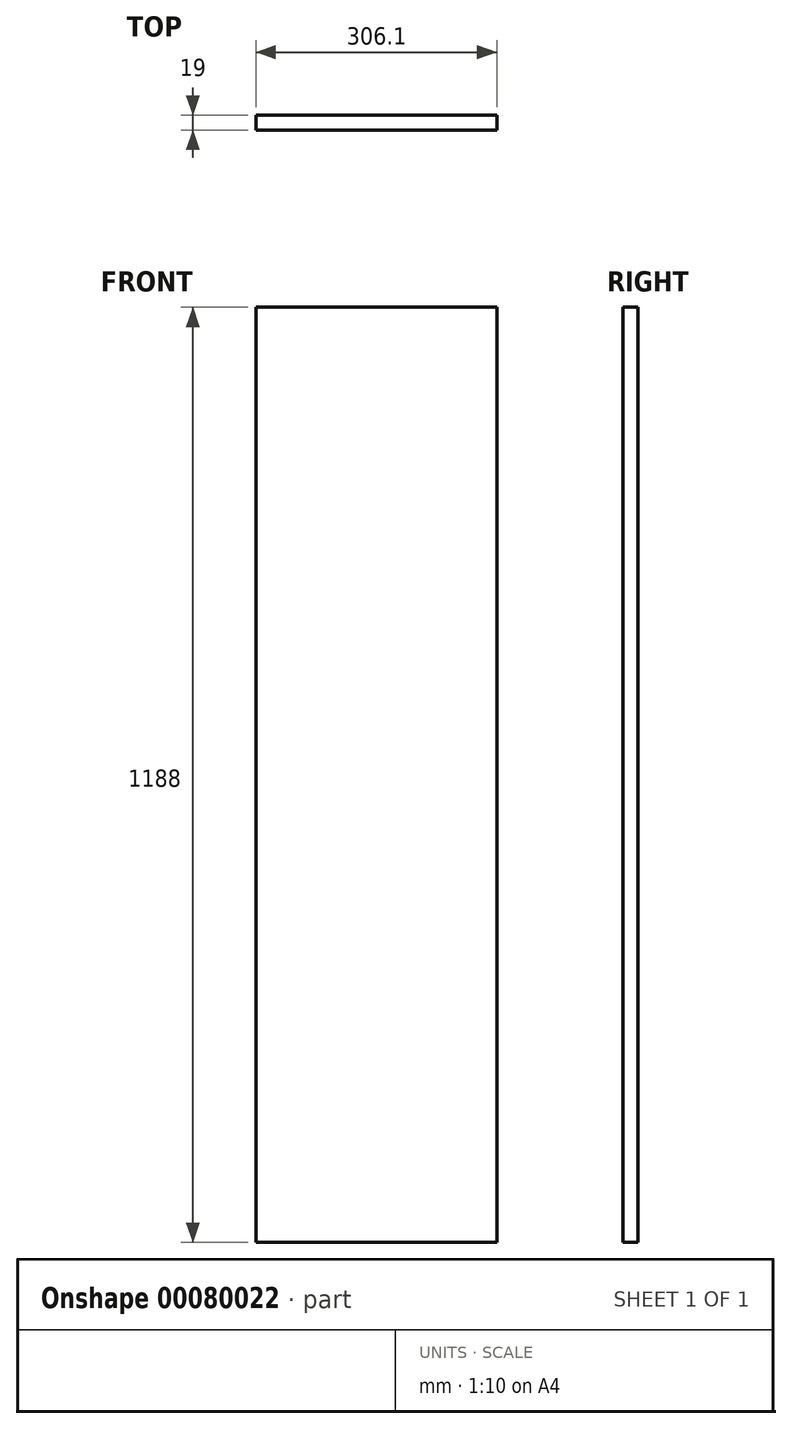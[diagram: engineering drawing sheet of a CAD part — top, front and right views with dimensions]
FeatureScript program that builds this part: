
annotation { "Feature Type Name" : "Feature", "Feature Type Description" : "" }
export const myFeature = defineFeature(function(context is Context, id is Id, definition is map)
    precondition{}
    {
        {
            var Q0;
            Q0=qCreatedBy(makeId("Front.planeOp"),FACE);
            var sketch = newSketch(context, id + "F0", { "sketchPlane" : qUnion([Q0])});
            skLineSegment(sketch, "E0.bottom", {"start": v(0, 0) * mm, "end": v(306.1, 0) * mm});
            skLineSegment(sketch, "E0.top", {"start": v(0, -1188) * mm, "end": v(306.1, -1188) * mm});
            skLineSegment(sketch, "E0.left", {"start": v(0, 0) * mm, "end": v(0, -1188) * mm});
            skLineSegment(sketch, "E0.right", {"start": v(306.1, 0) * mm, "end": v(306.1, -1188) * mm});
            skSolve(sketch);
        }
        {
            var Q0;
            Q0 = qSketchRegion(id + "F0", true);
            extrude(context, id + "F1", {"entities" : qUnion([Q0]), "depth" : 19 * mm});
        }
    });
